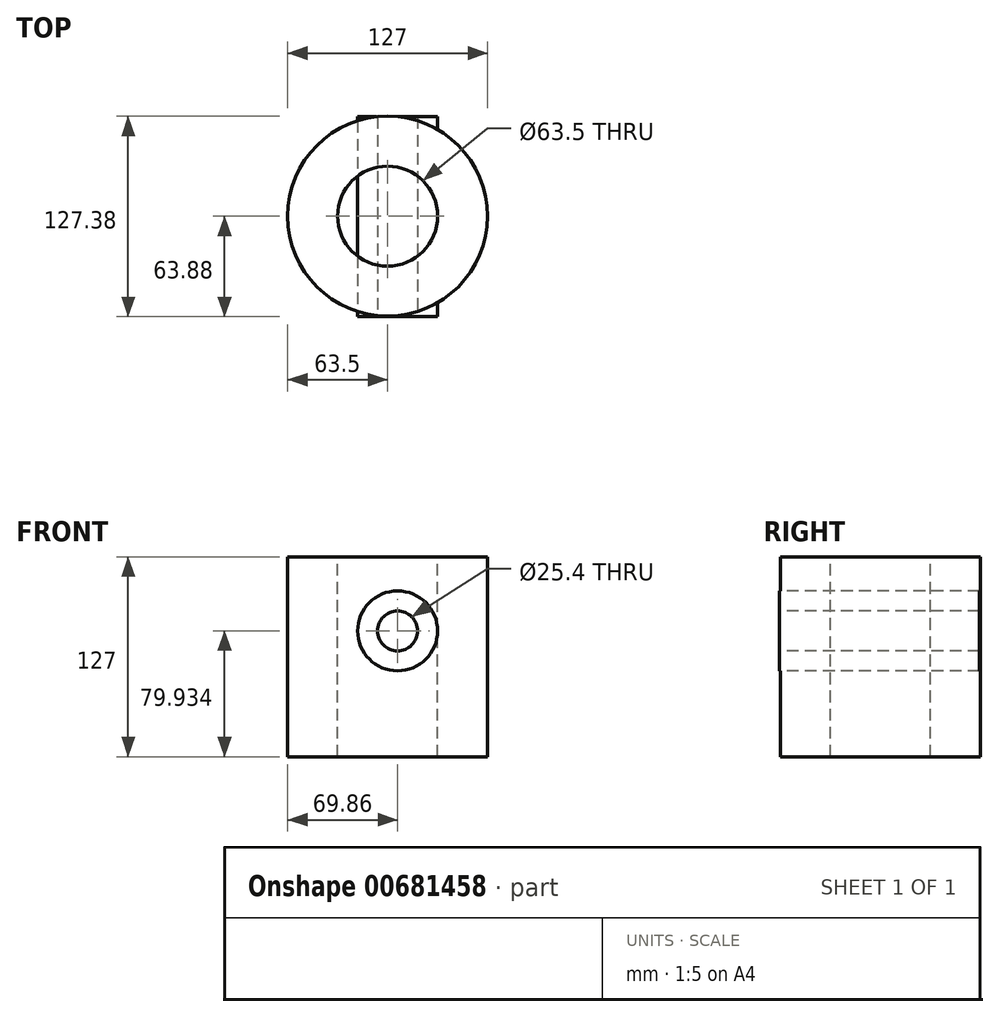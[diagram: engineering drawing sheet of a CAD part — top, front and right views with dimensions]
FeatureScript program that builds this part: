
annotation { "Feature Type Name" : "Feature", "Feature Type Description" : "" }
export const myFeature = defineFeature(function(context is Context, id is Id, definition is map)
    precondition{}
    {
        {
            var Q0;
            Q0=qCreatedBy(makeId("Front.planeOp"),FACE);
            var sketch = newSketch(context, id + "F0", { "sketchPlane" : qUnion([Q0])});
            skLineSegment(sketch, "E0.bottom", {"start": v(-69.86, 61) * mm, "end": v(-6.36, 61) * mm});
            skLineSegment(sketch, "E0.top", {"start": v(-69.86, -66) * mm, "end": v(-6.36, -66) * mm});
            skLineSegment(sketch, "E0.left", {"start": v(-69.86, 61) * mm, "end": v(-69.86, -66) * mm});
            skLineSegment(sketch, "E0.right", {"start": v(-6.36, 61) * mm, "end": v(-6.36, -66) * mm});
            skLineSegment(sketch, "E1", {"start": v(-38.11, 61) * mm, "end": v(-38.11, -66) * mm});
            skSolve(sketch);
        }
        {
            var Q0;
            {var subQ0=sQuery(id+"F0.wireOp",EDGE,"E0.left");Q0=makeQuery(id+"F0.imprint","IMPRINT",FACE,{"disambiguationData":[TD([[makeQuery(id+"F0.imprint","IMPRINT",EDGE,{"derivedFrom":subQ0}),1.0]])]});}
            var Q1;
            Q1=sQuery(id+"F0.wireOp",EDGE,"E0.right");
            revolve(context, id + "F1", {"entities" : qUnion([Q0]), "axis" : qUnion([Q1]), "revolveType" : RevolveType.FULL});
        }
        {
            var Q0;
            Q0=qCreatedBy(makeId("Right.planeOp"),FACE);
            var sketch = newSketch(context, id + "F2", { "sketchPlane" : qUnion([Q0])});
            skLineSegment(sketch, "E2.bottom", {"start": v(-63.88, 39.32) * mm, "end": v(63.12, 39.32) * mm});
            skLineSegment(sketch, "E2.top", {"start": v(-63.88, 13.92) * mm, "end": v(63.12, 13.92) * mm});
            skLineSegment(sketch, "E2.left", {"start": v(-63.88, 39.32) * mm, "end": v(-63.88, 13.92) * mm});
            skLineSegment(sketch, "E2.right", {"start": v(63.12, 39.32) * mm, "end": v(63.12, 13.92) * mm});
            skLineSegment(sketch, "E3", {"start": v(-63.88, 26.62) * mm, "end": v(63.12, 26.62) * mm});
            skSolve(sketch);
        }
        {
            var Q0;
            {var subQ0=sQuery(id+"F2.wireOp",EDGE,"E2.bottom");Q0=makeQuery(id+"F2.imprint","IMPRINT",FACE,{"disambiguationData":[TD([[makeQuery(id+"F2.imprint","IMPRINT",EDGE,{"derivedFrom":subQ0}),-1.0]])]});}
            var Q1;
            Q1=sQuery(id+"F2.wireOp",EDGE,"E2.top");
            revolve(context, id + "F3", {"entities" : qUnion([Q0]), "axis" : qUnion([Q1]), "revolveType" : RevolveType.FULL});
        }
    });
